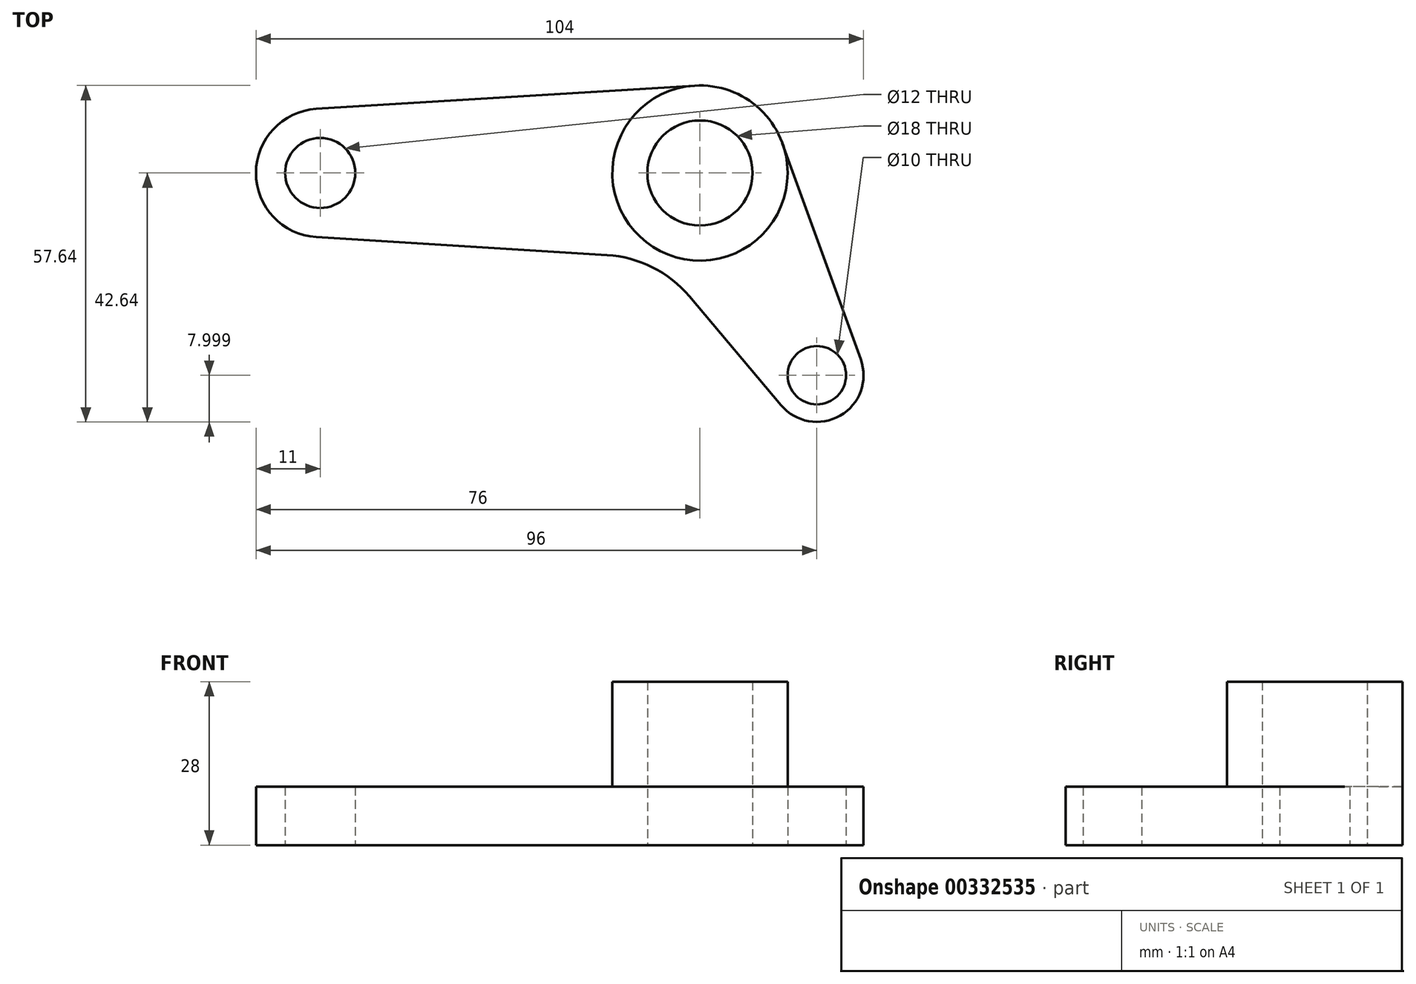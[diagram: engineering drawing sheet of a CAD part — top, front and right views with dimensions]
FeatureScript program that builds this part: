
annotation { "Feature Type Name" : "Feature", "Feature Type Description" : "" }
export const myFeature = defineFeature(function(context is Context, id is Id, definition is map)
    precondition{}
    {
        {
            var Q0;
            Q0=qCreatedBy(makeId("Top.planeOp"),FACE);
            var sketch = newSketch(context, id + "F0", { "sketchPlane" : qUnion([Q0])});
            skCircle(sketch, "E0", {"center": v(0, 0) * mm, "radius": 9 * mm});
            skCircle(sketch, "E1", {"center": v(0, 0) * mm, "radius": 15 * mm});
            skPoint(sketch, "E2", {"position": v(-65, 0) * mm});
            skCircle(sketch, "E3", {"center": v(-65, 0) * mm, "radius": 6 * mm});
            skArc(sketch, "E4", {"start": v(-65.68, 10.98) * mm, "mid": v(-76, 0) * mm, "end": v(-65.68, -10.98) * mm});
            skLineSegment(sketch, "E5", {"start": v(-65.68, 10.98) * mm, "end": v(-0.92, 14.97) * mm});
            skLineSegment(sketch, "E6", {"start": v(0, 0) * mm, "end": v(4.5, -7.8) * mm});
            skPoint(sketch, "E7", {"position": v(20, -34.64) * mm});
            skCircle(sketch, "E8", {"center": v(20, -34.64) * mm, "radius": 5 * mm});
            skArc(sketch, "E9", {"start": v(13.88, -39.8) * mm, "mid": v(24, -41.57) * mm, "end": v(27.52, -31.92) * mm});
            skLineSegment(sketch, "E10.MirrorCS", {"start": v(-65.68, -10.98) * mm, "end": v(-15.9, -14.05) * mm});
            skLineSegment(sketch, "E11", {"start": v(14.1, 5.11) * mm, "end": v(27.52, -31.92) * mm});
            skLineSegment(sketch, "E12.MirrorCS", {"start": v(-1.82, -21.13) * mm, "end": v(13.88, -39.8) * mm});
            skPoint(sketch, "E13.newPointA", {"position": v(-16.38, -3.83) * mm});
            skPoint(sketch, "E13.newPointB", {"position": v(6.34, -15.42) * mm});
            skArc(sketch, "E13.filletArc", {"start": v(-1.82, -21.13) * mm, "mid": v(-8.13, -16.15) * mm, "end": v(-15.9, -14.05) * mm});
            skPoint(sketch, "E14.orphan", {"position": v(17.64, -44.26) * mm});
            skPoint(sketch, "E15.orphan", {"position": v(29.5, -37.4) * mm});
            skPoint(sketch, "E16.orphan", {"position": v(11.5, 12.28) * mm});
            skPoint(sketch, "E17.orphan", {"position": v(6.34, 15.42) * mm});
            skSolve(sketch);
        }
        {
            var Q0;
            Q0 = qSketchRegion(id + "F0", true);
            extrude(context, id + "F1", {"entities" : qUnion([Q0]), "depth" : 10 * mm});
        }
        {
            var Q0;
            Q0=makeQuery(id+"F0.imprint","IMPRINT",FACE,{"disambiguationData":[TD([[makeQuery(id+"F0.imprint","IMPRINT",EDGE,{"derivedFrom":sQuery(id+"F0.wireOp",EDGE,"E0")}),-1.0]])]});
            extrude(context, id + "F2", {"entities" : qUnion([Q0]), "operationType" : NewBodyOperationType.ADD, "depth" : 28 * mm});
        }
    });
